# Revit family: Accessory-Towel_Ring-KALLISTA-Script-P25013_1
name_source: partatom
category: Specialty Equipment
units: mm (PartAtom-declared; Revit-internal decimal feet)

## family parameters
Cut with Voids When Loaded = No
Host = Face
OmniClass Number = 23.31.25.25
OmniClass Title = Towel Bars
Part Type = Normal
Room Calculation Point = No
Round Connector Dimension = Use Diameter
Shared = No

## types (6) — shared parameters
ADA Compliant = No
Assembly Code = C1030200
Date Modified = 10/19/2022
Default Elevation = 42"
Description = TOWEL RING
Height = 5 3/8"
Length = 6 15/16"
Manufacturer = Kallista Co.
Master Format 2014 = 10 28 00
Master Format 2014 Name = Toilet, Bath, and Laundry Accessories
Material = Solid Metal Construction
Product Documentation Link = https://resources.kohler.com
Product Name = SCRIPT
URL = https://www.kallista.com
WaterSense Certified = No
Width = 3"

## per-type parameters (varying)
| type | Finish | Model | Product Page URL | Type |
| AD-Nickel Silver | Kallista-Metal-AD-Nickel_Silver | P25013-00-AD | https://www.kallista.com | 1 |
| BAF-Brushed French Gold | Kallista-Metal-BAF-Brushed_French_Gold | P25013-00-BAF | https://www.kallista.com | 2 |
| BN-Brushed Nickel | Kallista-Metal-BN-Brushed_Nickel | P25013-00-BN |  | 3 |
| BV-Brushed Bronze | Kallista-Metal-BV-Brushed_Bronze | P25013-00-BV | https://www.kallista.com | 4 |
| CP-Chrome | Kallista-Metal-CP-Chrome | P25013-00-CP | https://www.kallista.com | 5 |
| SN-Polished Nickel | Kallista-Metal-SN-Polished_Nickel | P25013-00-SN | https://www.kallista.com | 6 |

## geometry (parser evidence)
native form markers: Sweep x6
no freeform markers — native parametric forms only
